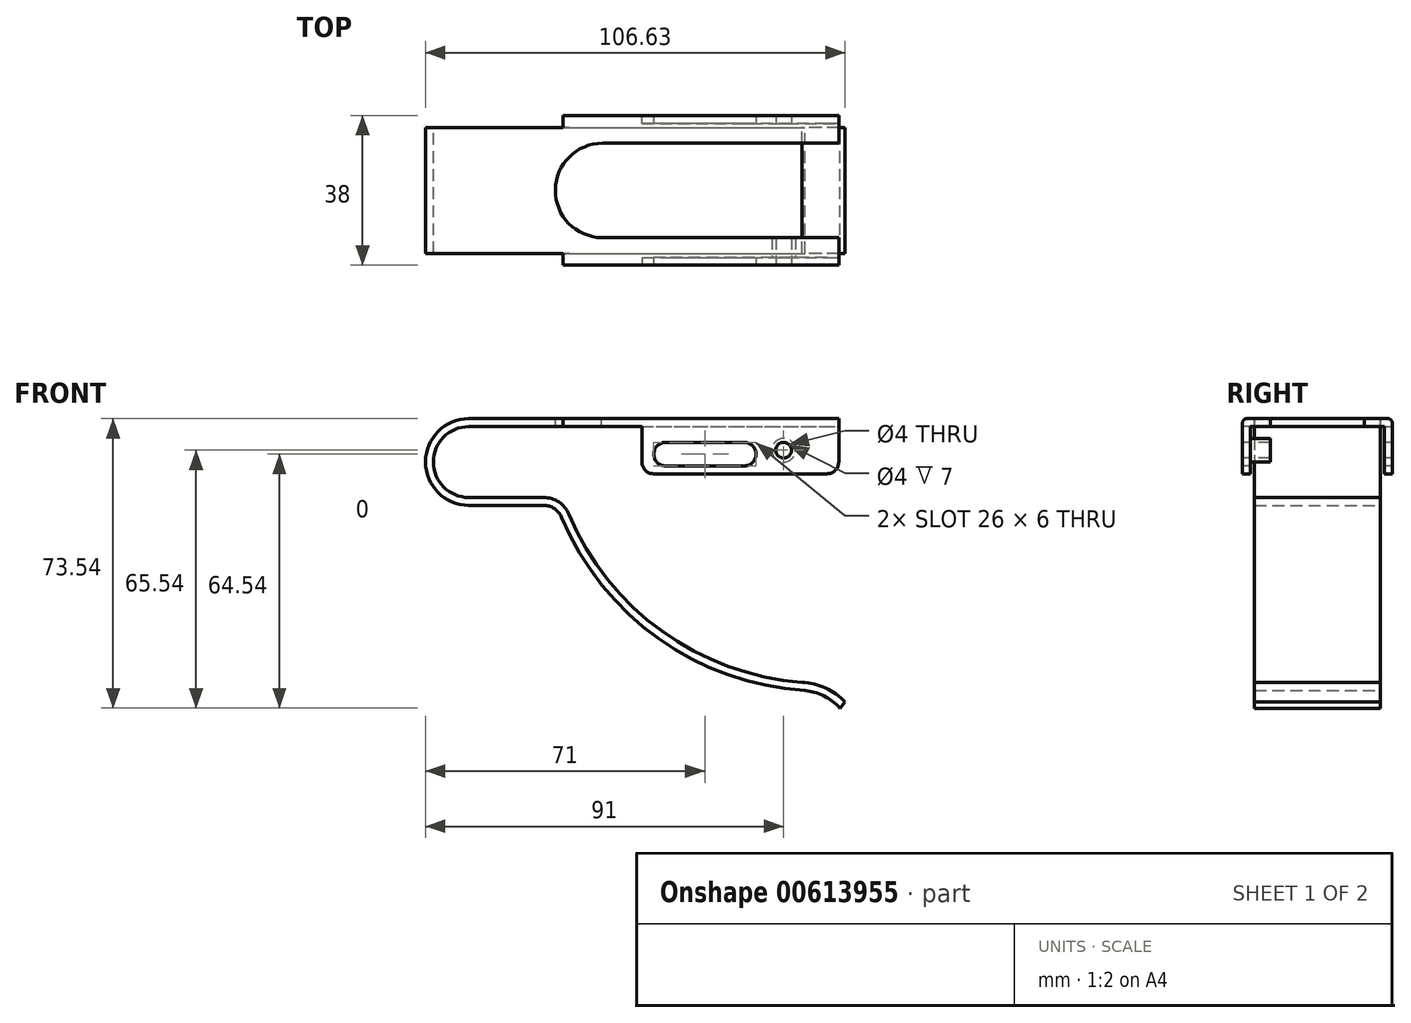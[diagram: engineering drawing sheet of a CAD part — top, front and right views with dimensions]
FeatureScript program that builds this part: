
annotation { "Feature Type Name" : "Feature", "Feature Type Description" : "" }
export const myFeature = defineFeature(function(context is Context, id is Id, definition is map)
    precondition{}
    {
        {
            var Q0;
            Q0=qCreatedBy(makeId("Front.planeOp"),FACE);
            var sketch = newSketch(context, id + "F0", { "sketchPlane" : qUnion([Q0])});
            skArc(sketch, "E0", {"start": v(0, 11) * mm, "mid": v(-11, 0) * mm, "end": v(0, -11) * mm});
            skLineSegment(sketch, "E1", {"start": v(0, 11) * mm, "end": v(94, 11) * mm});
            skLineSegment(sketch, "E2", {"start": v(0, -11) * mm, "end": v(19, -11) * mm});
            skArc(sketch, "E3", {"start": v(23.61, -14.06) * mm, "mid": v(48.23, -44.84) * mm, "end": v(85.36, -58.05) * mm});
            skArc(sketch, "E4", {"start": v(94.34, -62.54) * mm, "mid": v(90.27, -59.47) * mm, "end": v(85.36, -58.05) * mm});
            skPoint(sketch, "E5.visualSharp", {"position": v(22.4, -11) * mm});
            skArc(sketch, "E5.filletArc", {"start": v(23.61, -14.06) * mm, "mid": v(21.77, -11.84) * mm, "end": v(19, -11) * mm});
            skLineSegment(sketch, "E6.0", {"start": v(0, 9) * mm, "end": v(94, 9) * mm});
            skArc(sketch, "E6.1", {"start": v(0, 9) * mm, "mid": v(-9, 0) * mm, "end": v(0, -9) * mm});
            skArc(sketch, "E6.2", {"start": v(95.63, -61) * mm, "mid": v(90.65, -57.44) * mm, "end": v(84.7, -56) * mm});
            skArc(sketch, "E6.3", {"start": v(25.45, -13.3) * mm, "mid": v(49.07, -42.99) * mm, "end": v(84.7, -56) * mm});
            skArc(sketch, "E6.4", {"start": v(25.45, -13.3) * mm, "mid": v(22.88, -10.17) * mm, "end": v(19, -9) * mm});
            skLineSegment(sketch, "E6.5", {"start": v(0, -9) * mm, "end": v(19, -9) * mm});
            skLineSegment(sketch, "E7", {"start": v(94, 9) * mm, "end": v(94, 11) * mm});
            skLineSegment(sketch, "E8", {"start": v(94.34, -62.54) * mm, "end": v(95.63, -61) * mm});
            skLineSegment(sketch, "E9", {"start": v(95.63, -61) * mm, "end": v(102.4, -61) * mm, "construction": true});
            skSolve(sketch);
        }
        {
            var Q0;
            Q0 = qSketchRegion(id + "F0", true);
            extrude(context, id + "F1", {"entities" : qUnion([Q0]), "depth" : 16 * mm, "offsetDistance" : 25 * mm});
        }
        {
            var Q0;
            Q0=makeQuery(id+"F1.opExtrude","SWEPT_FACE",FACE,{"disambiguationData":[OSD([sQuery(id+"F0.wireOp",EDGE,"E1")])]});
            var sketch = newSketch(context, id + "F2", { "sketchPlane" : qUnion([Q0])});
            skLineSegment(sketch, "E10.bottom", {"start": v(24, -16) * mm, "end": v(94, -16) * mm});
            skLineSegment(sketch, "E10.top", {"start": v(24, -19) * mm, "end": v(94, -19) * mm});
            skLineSegment(sketch, "E10.left", {"start": v(24, -16) * mm, "end": v(24, -19) * mm});
            skLineSegment(sketch, "E10.right", {"start": v(94, -16) * mm, "end": v(94, -19) * mm});
            skSolve(sketch);
        }
        {
            var Q0;
            Q0 = qSketchRegion(id + "F2", true);
            extrude(context, id + "F3", {"entities" : qUnion([Q0]), "operationType" : NewBodyOperationType.ADD, "oppositeDirection" : true, "depth" : 2 * mm, "offsetDistance" : 25 * mm});
        }
        {
            var Q0;
            Q0=makeQuery(id+"F3.opExtrude","SWEPT_FACE",FACE,{"disambiguationData":[OSD([sQuery(id+"F2.wireOp",EDGE,"E10.top")])]});
            var sketch = newSketch(context, id + "F4", { "sketchPlane" : qUnion([Q0])});
            skLineSegment(sketch, "E11.bottom", {"start": v(94, 11) * mm, "end": v(44, 11) * mm});
            skLineSegment(sketch, "E11.top", {"start": v(94, -3) * mm, "end": v(44, -3) * mm});
            skLineSegment(sketch, "E11.left", {"start": v(94, 11) * mm, "end": v(94, -3) * mm});
            skLineSegment(sketch, "E11.right", {"start": v(44, 11) * mm, "end": v(44, -3) * mm});
            skSolve(sketch);
        }
        {
            var Q0;
            Q0 = qSketchRegion(id + "F4", true);
            extrude(context, id + "F5", {"entities" : qUnion([Q0]), "operationType" : NewBodyOperationType.ADD, "oppositeDirection" : true, "depth" : 2 * mm, "offsetDistance" : 25 * mm});
        }
        {
            var Q0;
            Q0=makeQuery(id+"F3.opExtrude","CAP_EDGE",EDGE,{"disambiguationData":[OSD([sQuery(id+"F2.wireOp",EDGE,"E10.top")])],"isStart":true});
            fillet(context, id + "F6", {"entities" : qUnion([Q0]), "radius" : 1 * mm, "allowEdgeOverflow" : false});
        }
        {
            var Q0;
            Q0=makeQuery(id+"F1.opExtrude","SWEPT_BODY",BODY,{"disambiguationData":[OSD([sQuery(id+"F0.wireOp",EDGE,"E0"),sQuery(id+"F0.wireOp",EDGE,"E1"),sQuery(id+"F0.wireOp",EDGE,"E2"),sQuery(id+"F0.wireOp",EDGE,"E3"),sQuery(id+"F0.wireOp",EDGE,"E4"),sQuery(id+"F0.wireOp",EDGE,"E5.filletArc"),sQuery(id+"F0.wireOp",EDGE,"E6.0"),sQuery(id+"F0.wireOp",EDGE,"E6.1"),sQuery(id+"F0.wireOp",EDGE,"E6.2"),sQuery(id+"F0.wireOp",EDGE,"E6.3"),sQuery(id+"F0.wireOp",EDGE,"E6.4"),sQuery(id+"F0.wireOp",EDGE,"E6.5"),sQuery(id+"F0.wireOp",EDGE,"E7"),sQuery(id+"F0.wireOp",EDGE,"E8")])]});
            var Q1;
            Q1=qCreatedBy(makeId("Front.planeOp"),FACE);
            mirror(context, id + "F7", {"operationType" : NewBodyOperationType.ADD, "entities" : qUnion([Q0]), "mirrorPlane" : qUnion([Q1])});
        }
        {
            var Q0;
            {var subQ0=makeQuery(id+"F3.boolean.opBoolean","MERGE",FACE,{"derivedFrom":[makeQuery(id+"F1.opExtrude","SWEPT_FACE",FACE,{"disambiguationData":[OSD([sQuery(id+"F0.wireOp",EDGE,"E1")])]}),makeQuery(id+"F3.opExtrude","CAP_FACE",FACE,{"disambiguationData":[OSD([sQuery(id+"F2.wireOp",EDGE,"E10.bottom"),sQuery(id+"F2.wireOp",EDGE,"E10.top"),sQuery(id+"F2.wireOp",EDGE,"E10.left"),sQuery(id+"F2.wireOp",EDGE,"E10.right")])],"isStart":true})]});Q0=makeQuery(id+"F7.boolean.opBoolean","MERGE",FACE,{"derivedFrom":[subQ0,makeQuery(id+"F7.opPattern","COPY",FACE,{"derivedFrom":subQ0,"instanceName":"1"})]});}
            var sketch = newSketch(context, id + "F8", { "sketchPlane" : qUnion([Q0])});
            skArc(sketch, "E12", {"start": v(34, 12) * mm, "mid": v(22, -0.1) * mm, "end": v(34.22, -12) * mm});
            skLineSegment(sketch, "E13", {"start": v(34, 12) * mm, "end": v(94, 12) * mm});
            skLineSegment(sketch, "E14", {"start": v(33.78, -12) * mm, "end": v(94, -12) * mm});
            skSolve(sketch);
        }
        {
            var Q0;
            {var subQ7=sQuery(id+"F8.wireOp",EDGE,"E13");Q0=makeQuery(id+"F8.imprint","IMPRINT",FACE,{"disambiguationData":[TD([[makeQuery(id+"F8.imprint","IMPRINT",EDGE,{"derivedFrom":subQ7}),-1.0]])]});}
            extrude(context, id + "F9", {"entities" : qUnion([Q0]), "operationType" : NewBodyOperationType.REMOVE, "oppositeDirection" : true, "depth" : 2 * mm, "offsetDistance" : 25 * mm});
        }
        {
            var Q0;
            Q0=makeQuery(id+"F5.boolean.opBoolean","MERGE",FACE,{"derivedFrom":[makeQuery(id+"F3.opExtrude","SWEPT_FACE",FACE,{"disambiguationData":[OSD([sQuery(id+"F2.wireOp",EDGE,"E10.top")])]}),makeQuery(id+"F5.opExtrude","CAP_FACE",FACE,{"disambiguationData":[OSD([sQuery(id+"F4.wireOp",EDGE,"E11.bottom"),sQuery(id+"F4.wireOp",EDGE,"E11.top"),sQuery(id+"F4.wireOp",EDGE,"E11.left"),sQuery(id+"F4.wireOp",EDGE,"E11.right")])],"isStart":true})]});
            var sketch = newSketch(context, id + "F10", { "sketchPlane" : qUnion([Q0])});
            skLineSegment(sketch, "E15", {"start": v(50, 2) * mm, "end": v(70, 2) * mm});
            skArc(sketch, "E16.0.startCap", {"start": v(50, -1) * mm, "mid": v(47, 2) * mm, "end": v(50, 5) * mm});
            skArc(sketch, "E16.0.endCap", {"start": v(70, 5) * mm, "mid": v(73, 2) * mm, "end": v(70, -1) * mm});
            skLineSegment(sketch, "E16.0.left", {"start": v(50, 5) * mm, "end": v(70, 5) * mm});
            skLineSegment(sketch, "E16.0.right", {"start": v(50, -1) * mm, "end": v(70, -1) * mm});
            skSolve(sketch);
        }
        {
            var Q0;
            Q0 = qSketchRegion(id + "F10", true);
            extrude(context, id + "F11", {"entities" : qUnion([Q0]), "operationType" : NewBodyOperationType.REMOVE, "endBound" : BoundingType.THROUGH_ALL, "oppositeDirection" : true, "depth" : 25 * mm, "offsetDistance" : 25 * mm});
        }
        {
            var Q0;
            Q0=makeQuery(id+"F5.boolean.opBoolean","MERGE",FACE,{"derivedFrom":[makeQuery(id+"F3.opExtrude","SWEPT_FACE",FACE,{"disambiguationData":[OSD([sQuery(id+"F2.wireOp",EDGE,"E10.top")])]}),makeQuery(id+"F5.opExtrude","CAP_FACE",FACE,{"disambiguationData":[OSD([sQuery(id+"F4.wireOp",EDGE,"E11.bottom"),sQuery(id+"F4.wireOp",EDGE,"E11.top"),sQuery(id+"F4.wireOp",EDGE,"E11.left"),sQuery(id+"F4.wireOp",EDGE,"E11.right")])],"isStart":true})]});
            var sketch = newSketch(context, id + "F12", { "sketchPlane" : qUnion([Q0])});
            skPoint(sketch, "E17", {"position": v(80, 3) * mm});
            skSolve(sketch);
        }
        {
            var Q0;
            Q0=sQuery(id+"F12.wireOp",VERTEX,"E17");
            var Q1;
            Q1=makeQuery(id+"F1.opExtrude","SWEPT_BODY",BODY,{"disambiguationData":[OSD([sQuery(id+"F0.wireOp",EDGE,"E0"),sQuery(id+"F0.wireOp",EDGE,"E1"),sQuery(id+"F0.wireOp",EDGE,"E2"),sQuery(id+"F0.wireOp",EDGE,"E3"),sQuery(id+"F0.wireOp",EDGE,"E4"),sQuery(id+"F0.wireOp",EDGE,"E5.filletArc"),sQuery(id+"F0.wireOp",EDGE,"E6.0"),sQuery(id+"F0.wireOp",EDGE,"E6.1"),sQuery(id+"F0.wireOp",EDGE,"E6.2"),sQuery(id+"F0.wireOp",EDGE,"E6.3"),sQuery(id+"F0.wireOp",EDGE,"E6.4"),sQuery(id+"F0.wireOp",EDGE,"E6.5"),sQuery(id+"F0.wireOp",EDGE,"E7"),sQuery(id+"F0.wireOp",EDGE,"E8")])]});
            hole(context, id + "F13", {"style" : HoleStyle.SIMPLE, "endStyle" : HoleEndStyle.THROUGH, "holeDiameter" : 4 * mm, "majorDiameter" : 5 * mm, "isTappedThrough" : true, "tappedDepth" : 12 * mm, "tapClearance" : 3, "locations" : qUnion([Q0]), "scope" : qUnion([Q1])});
        }
        {
            var Q0;
            Q0=makeQuery(id+"F5.opExtrude","CAP_FACE",FACE,{"disambiguationData":[OSD([sQuery(id+"F4.wireOp",EDGE,"E11.bottom"),sQuery(id+"F4.wireOp",EDGE,"E11.top"),sQuery(id+"F4.wireOp",EDGE,"E11.left"),sQuery(id+"F4.wireOp",EDGE,"E11.right")])],"isStart":false});
            var sketch = newSketch(context, id + "F14", { "sketchPlane" : qUnion([Q0])});
            skCircle(sketch, "E18.0", {"center": v(-80, 3) * mm, "radius": 2 * mm});
            skCircle(sketch, "E19.0", {"center": v(-80, 3) * mm, "radius": 3 * mm});
            skSolve(sketch);
        }
        {
            var Q0;
            Q0 = qSketchRegion(id + "F14", true);
            extrude(context, id + "F15", {"entities" : qUnion([Q0]), "operationType" : NewBodyOperationType.ADD, "depth" : 5 * mm, "offsetDistance" : 25 * mm});
        }
        {
            var Q0;
            Q0=makeQuery(id+"F5.opExtrude","SWEPT_EDGE",EDGE,{"disambiguationData":[OSD([sQuery(id+"F4.wireOp",EDGE,"E11.top"),sQuery(id+"F4.wireOp",EDGE,"E11.left")])]});
            var Q1;
            Q1=makeQuery(id+"F5.opExtrude","SWEPT_EDGE",EDGE,{"disambiguationData":[OSD([sQuery(id+"F4.wireOp",EDGE,"E11.top"),sQuery(id+"F4.wireOp",EDGE,"E11.right")])]});
            var Q2;
            Q2=makeQuery(id+"F7.opPattern","COPY",EDGE,{"derivedFrom":makeQuery(id+"F5.opExtrude","SWEPT_EDGE",EDGE,{"disambiguationData":[OSD([sQuery(id+"F4.wireOp",EDGE,"E11.top"),sQuery(id+"F4.wireOp",EDGE,"E11.right")])]}),"instanceName":"1"});
            var Q3;
            Q3=makeQuery(id+"F7.opPattern","COPY",EDGE,{"derivedFrom":makeQuery(id+"F5.opExtrude","SWEPT_EDGE",EDGE,{"disambiguationData":[OSD([sQuery(id+"F4.wireOp",EDGE,"E11.top"),sQuery(id+"F4.wireOp",EDGE,"E11.left")])]}),"instanceName":"1"});
            fillet(context, id + "F16", {"entities" : qUnion([Q0, Q1, Q2, Q3]), "radius" : 3 * mm, "tangentPropagation" : true, "allowEdgeOverflow" : false});
        }
    });
